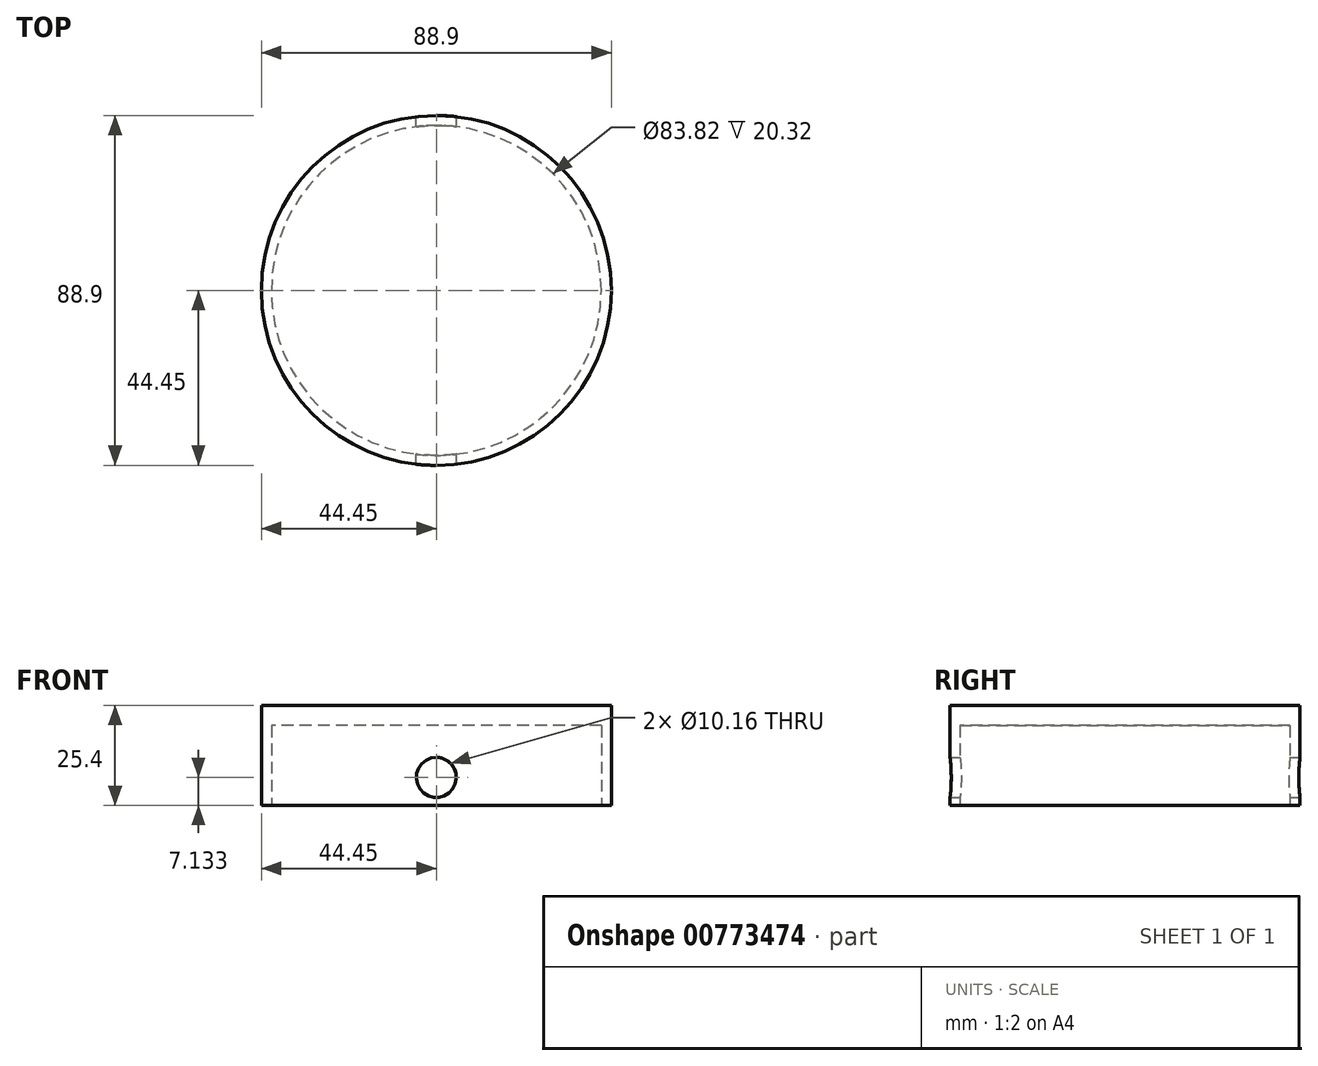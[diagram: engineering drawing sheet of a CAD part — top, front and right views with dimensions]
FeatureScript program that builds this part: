
annotation { "Feature Type Name" : "Feature", "Feature Type Description" : "" }
export const myFeature = defineFeature(function(context is Context, id is Id, definition is map)
    precondition{}
    {
        {
            var Q0;
            Q0=qCreatedBy(makeId("Top.planeOp"),FACE);
            var sketch = newSketch(context, id + "F0", { "sketchPlane" : qUnion([Q0])});
            skCircle(sketch, "E0", {"center": v(0, 0) * mm, "radius": 44.45 * mm});
            skCircle(sketch, "E1", {"center": v(0, 0) * mm, "radius": 41.91 * mm});
            skSolve(sketch);
        }
        {
            var Q0;
            Q0=makeQuery(id+"F0.imprint","IMPRINT",FACE,{"disambiguationData":[TD([[makeQuery(id+"F0.imprint","IMPRINT",EDGE,{"derivedFrom":sQuery(id+"F0.wireOp",EDGE,"E0")}),1.0]])]});
            extrude(context, id + "F1", {"entities" : qUnion([Q0]), "depth" : 25.4 * mm, "offsetDistance" : 25.4 * mm});
        }
        {
            var Q0;
            Q0=makeQuery(id+"F1.opExtrude","CAP_FACE",FACE,{"disambiguationData":[OSD([sQuery(id+"F0.wireOp",EDGE,"E0"),sQuery(id+"F0.wireOp",EDGE,"E1")])],"isStart":false});
            var sketch = newSketch(context, id + "F2", { "sketchPlane" : qUnion([Q0])});
            skCircle(sketch, "E2", {"center": v(0, 0) * mm, "radius": 38.1 * mm});
            skSolve(sketch);
        }
        {
            var Q0;
            Q0=makeQuery(id+"F2.imprint","IMPRINT",FACE,{"disambiguationData":[TD([[makeQuery(id+"F2.imprint","IMPRINT",EDGE,{"derivedFrom":makeQuery(id+"F1.opExtrude","CAP_EDGE",EDGE,{"disambiguationData":[OSD([sQuery(id+"F0.wireOp",EDGE,"E1")])],"isStart":false})}),1.0]])]});
            var Q1;
            Q1=makeQuery(id+"F2.imprint","IMPRINT",FACE,{"disambiguationData":[TD([[makeQuery(id+"F2.imprint","IMPRINT",EDGE,{"derivedFrom":sQuery(id+"F2.wireOp",EDGE,"E2")}),1.0]])]});
            extrude(context, id + "F3", {"entities" : qUnion([Q0, Q1]), "operationType" : NewBodyOperationType.ADD, "oppositeDirection" : true, "depth" : 5.08 * mm, "offsetDistance" : 25.4 * mm});
        }
        {
            var Q0;
            Q0=qCreatedBy(makeId("Front.planeOp"),FACE);
            var sketch = newSketch(context, id + "F4", { "sketchPlane" : qUnion([Q0])});
            skCircle(sketch, "E3", {"center": v(0, 7.13) * mm, "radius": 5.08 * mm});
            skSolve(sketch);
        }
        {
            var Q0;
            Q0=makeQuery(id+"F4.imprint","IMPRINT",FACE,{"disambiguationData":[TD([[makeQuery(id+"F4.imprint","IMPRINT",EDGE,{"derivedFrom":sQuery(id+"F4.wireOp",EDGE,"E3")}),1.0]])]});
            extrude(context, id + "F5", {"entities" : qUnion([Q0]), "operationType" : NewBodyOperationType.REMOVE, "endBound" : BoundingType.SYMMETRIC, "depth" : 113.28 * mm, "offsetDistance" : 25.4 * mm});
        }
    });
